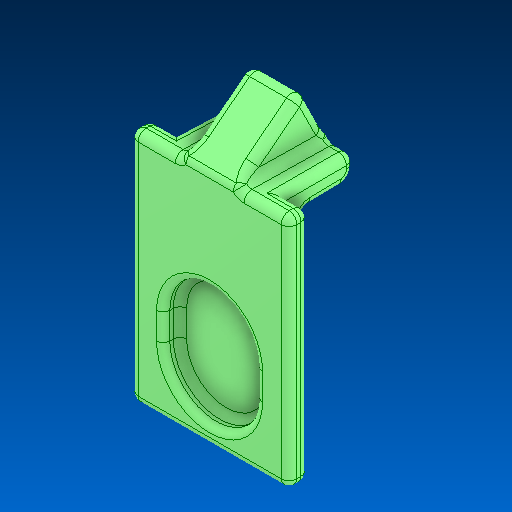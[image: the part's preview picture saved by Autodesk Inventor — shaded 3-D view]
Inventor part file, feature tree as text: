
AUTODESK INVENTOR PART (.ipt)
format: ipt  version: 2022.2 (Build 262287000, 287)  size: 274,432 bytes
history: native  units: in
note: dims shown in document units (in); Inventor stores cm internally (conversion verified against a paired STEP export)
features: fillet x1
ambient origin geometry x8: Origin, YZ Plane, XZ Plane, XY Plane, X Axis, Y Axis, Z Axis, Center Point
bodies: Solid1 (feature_tree)
feature tree (1):
  fillet  "Fillet4"  [1 undecoded]
note: 1 required parameter value undecoded (feature->parameter linkage not recoverable at this tier; creation-order binding heuristic only, values carry confidence <= 0.55)
